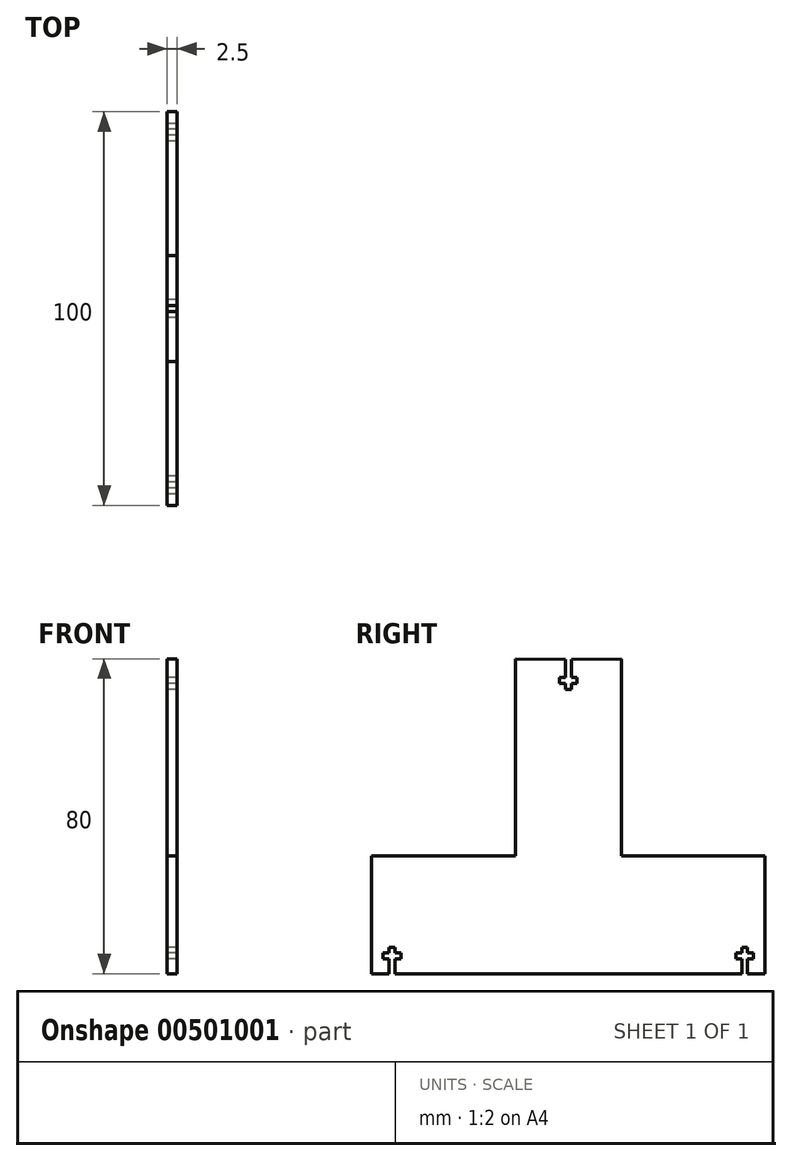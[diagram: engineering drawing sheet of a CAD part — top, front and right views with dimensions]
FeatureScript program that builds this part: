
annotation { "Feature Type Name" : "Feature", "Feature Type Description" : "" }
export const myFeature = defineFeature(function(context is Context, id is Id, definition is map)
    precondition{}
    {
        {
            var Q0;
            Q0=qCreatedBy(makeId("Right.planeOp"),FACE);
            var sketch = newSketch(context, id + "F0", { "sketchPlane" : qUnion([Q0])});
            skLineSegment(sketch, "E0", {"start": v(50, -0.01) * mm, "end": v(50, 29.99) * mm});
            skLineSegment(sketch, "E1", {"start": v(50, 29.99) * mm, "end": v(13.48, 29.99) * mm});
            skLineSegment(sketch, "E2", {"start": v(13.48, 29.99) * mm, "end": v(13.48, 79.99) * mm});
            skLineSegment(sketch, "E3", {"start": v(0, 42.5) * mm, "end": v(0, 0) * mm, "construction": true});
            skLineSegment(sketch, "E4.MirrorCS", {"start": v(-50, -0.01) * mm, "end": v(-50, 29.99) * mm});
            skLineSegment(sketch, "E5.MirrorCS", {"start": v(-50, 29.99) * mm, "end": v(-13.48, 29.99) * mm});
            skLineSegment(sketch, "E6.MirrorCS", {"start": v(-13.48, 29.99) * mm, "end": v(-13.48, 79.99) * mm});
            skLineSegment(sketch, "E7", {"start": v(-45.56, 0) * mm, "end": v(-45.56, 3.74) * mm});
            skLineSegment(sketch, "E8", {"start": v(-45.56, 3.74) * mm, "end": v(-47.06, 3.74) * mm});
            skLineSegment(sketch, "E9", {"start": v(-47.06, 3.74) * mm, "end": v(-47.06, 5.24) * mm});
            skLineSegment(sketch, "E10", {"start": v(-47.06, 5.24) * mm, "end": v(-45.56, 5.24) * mm});
            skLineSegment(sketch, "E11", {"start": v(-45.56, 5.24) * mm, "end": v(-45.56, 6.74) * mm});
            skLineSegment(sketch, "E12", {"start": v(-45.56, 6.74) * mm, "end": v(-44.06, 6.74) * mm});
            skLineSegment(sketch, "E13", {"start": v(-44.06, 6.74) * mm, "end": v(-44.06, 5.24) * mm});
            skLineSegment(sketch, "E14", {"start": v(-44.06, 5.24) * mm, "end": v(-42.56, 5.24) * mm});
            skLineSegment(sketch, "E15", {"start": v(-42.56, 5.24) * mm, "end": v(-42.56, 3.74) * mm});
            skLineSegment(sketch, "E16", {"start": v(-42.56, 3.74) * mm, "end": v(-44.06, 3.74) * mm});
            skLineSegment(sketch, "E17", {"start": v(-44.06, 3.74) * mm, "end": v(-44.06, 0) * mm});
            skLineSegment(sketch, "E18", {"start": v(-50, -0.01) * mm, "end": v(-45.56, 0) * mm});
            skLineSegment(sketch, "E19", {"start": v(-44.06, 0) * mm, "end": v(0, 0) * mm});
            skLineSegment(sketch, "E20.MirrorCS", {"start": v(42.56, 3.74) * mm, "end": v(44.06, 3.74) * mm});
            skLineSegment(sketch, "E21.MirrorCS", {"start": v(47.06, 3.74) * mm, "end": v(47.06, 5.24) * mm});
            skLineSegment(sketch, "E22.MirrorCS", {"start": v(45.56, 6.74) * mm, "end": v(44.06, 6.74) * mm});
            skLineSegment(sketch, "E23.MirrorCS", {"start": v(44.06, 6.74) * mm, "end": v(44.06, 5.24) * mm});
            skLineSegment(sketch, "E24.MirrorCS", {"start": v(44.06, 5.24) * mm, "end": v(42.56, 5.24) * mm});
            skLineSegment(sketch, "E25.MirrorCS", {"start": v(47.06, 5.24) * mm, "end": v(45.56, 5.24) * mm});
            skLineSegment(sketch, "E26.MirrorCS", {"start": v(45.56, 0) * mm, "end": v(45.56, 3.74) * mm});
            skLineSegment(sketch, "E27.MirrorCS", {"start": v(44.06, 3.74) * mm, "end": v(44.06, 0) * mm});
            skLineSegment(sketch, "E28.MirrorCS", {"start": v(42.56, 5.24) * mm, "end": v(42.56, 3.74) * mm});
            skLineSegment(sketch, "E29.MirrorCS", {"start": v(45.56, 3.74) * mm, "end": v(47.06, 3.74) * mm});
            skLineSegment(sketch, "E30.MirrorCS", {"start": v(45.56, 5.24) * mm, "end": v(45.56, 6.74) * mm});
            skLineSegment(sketch, "E31", {"start": v(0, 0) * mm, "end": v(44.06, 0) * mm});
            skLineSegment(sketch, "E32", {"start": v(45.56, 0) * mm, "end": v(50, -0.01) * mm});
            skLineSegment(sketch, "E33", {"start": v(0.74, 79.91) * mm, "end": v(0.74, 75.23) * mm});
            skLineSegment(sketch, "E34", {"start": v(0.74, 75.23) * mm, "end": v(2.24, 75.23) * mm});
            skLineSegment(sketch, "E35", {"start": v(2.24, 75.23) * mm, "end": v(2.24, 73.73) * mm});
            skLineSegment(sketch, "E36", {"start": v(2.24, 73.73) * mm, "end": v(0.74, 73.73) * mm});
            skLineSegment(sketch, "E37", {"start": v(0.74, 73.73) * mm, "end": v(0.74, 72.23) * mm});
            skLineSegment(sketch, "E38", {"start": v(0.74, 72.23) * mm, "end": v(-0.76, 72.23) * mm});
            skLineSegment(sketch, "E39", {"start": v(-0.76, 72.23) * mm, "end": v(-0.76, 73.73) * mm});
            skLineSegment(sketch, "E40", {"start": v(-0.76, 73.73) * mm, "end": v(-2.26, 73.73) * mm});
            skLineSegment(sketch, "E41", {"start": v(-2.26, 73.73) * mm, "end": v(-2.26, 75.23) * mm});
            skLineSegment(sketch, "E42", {"start": v(-2.26, 75.23) * mm, "end": v(-0.76, 75.23) * mm});
            skLineSegment(sketch, "E43", {"start": v(-0.76, 75.23) * mm, "end": v(-0.76, 79.91) * mm});
            skLineSegment(sketch, "E44", {"start": v(-13.48, 79.99) * mm, "end": v(-0.76, 79.91) * mm});
            skLineSegment(sketch, "E45", {"start": v(0.74, 79.91) * mm, "end": v(13.48, 79.99) * mm});
            skSolve(sketch);
        }
        {
            var Q0;
            Q0=makeQuery(id+"F0.imprint","IMPRINT",FACE,{"disambiguationData":[TD([[makeQuery(id+"F0.imprint","IMPRINT",EDGE,{"derivedFrom":sQuery(id+"F0.wireOp",EDGE,"Y3s8OWVh-kGGm-R7xk-UbSu-pdOVKzQd29nt")}),1.0]])]});
            var Q1;
            Q1=makeQuery(id+"F0.imprint","IMPRINT",FACE,{"disambiguationData":[TD([[makeQuery(id+"F0.imprint","IMPRINT",EDGE,{"derivedFrom":sQuery(id+"F0.wireOp",EDGE,"E0")}),1.0]])]});
            extrude(context, id + "F1", {"entities" : qUnion([Q0, Q1]), "depth" : 2.5 * mm, "offsetDistance" : 25 * mm});
        }
    });
